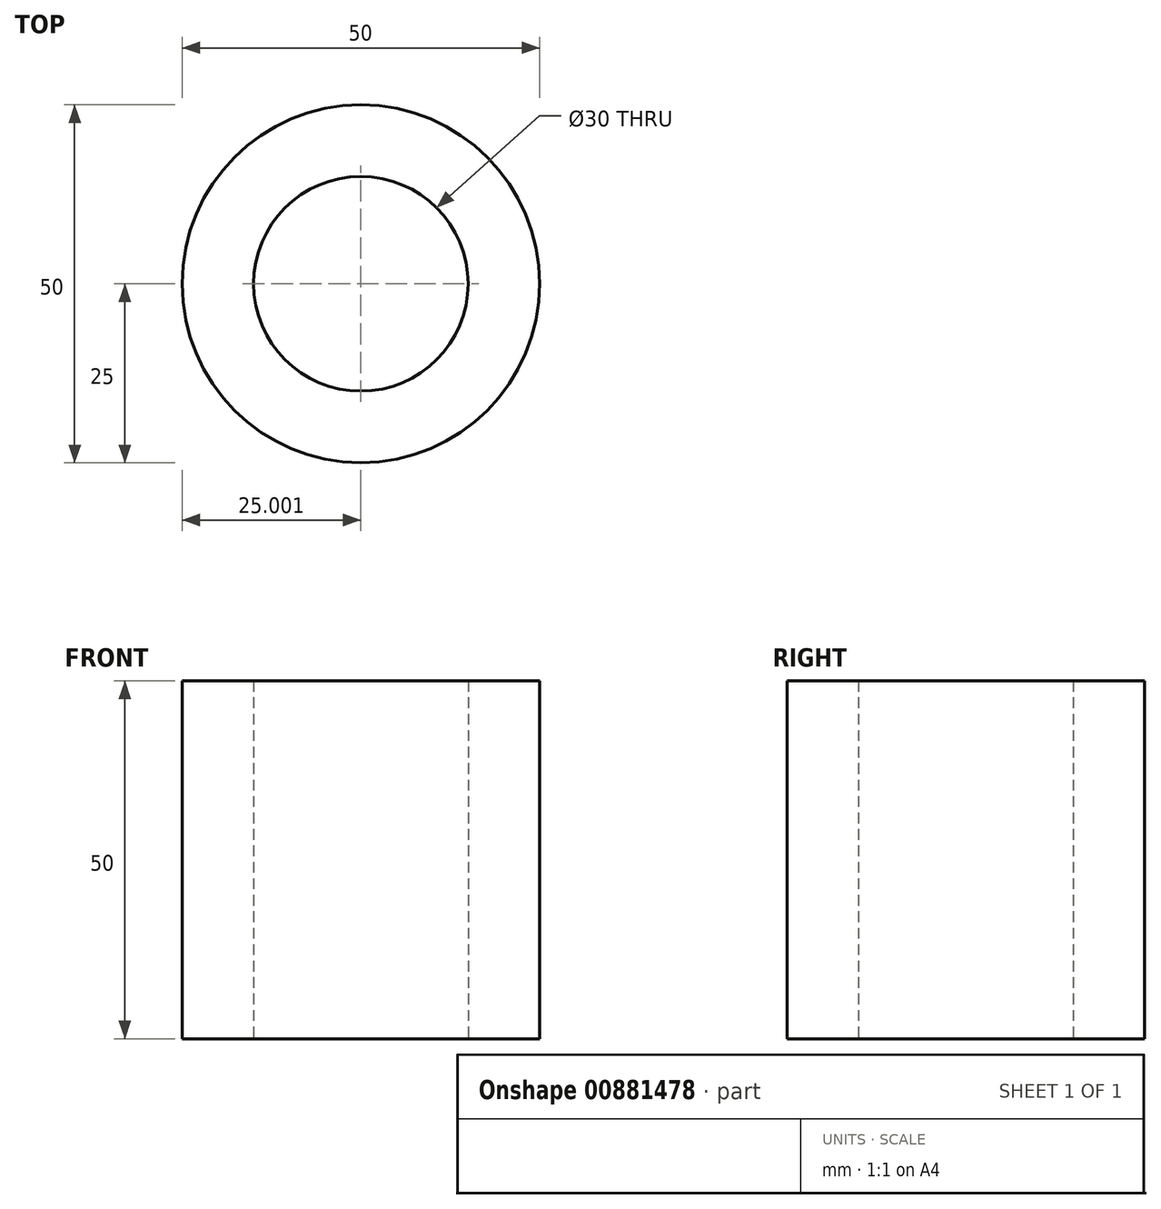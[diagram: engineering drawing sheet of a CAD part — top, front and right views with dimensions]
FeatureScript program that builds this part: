
annotation { "Feature Type Name" : "Feature", "Feature Type Description" : "" }
export const myFeature = defineFeature(function(context is Context, id is Id, definition is map)
    precondition{}
    {
        {
            var Q0;
            Q0=qCreatedBy(makeId("Top.planeOp"),FACE);
            var sketch = newSketch(context, id + "F0", { "sketchPlane" : qUnion([Q0])});
            skCircle(sketch, "E0", {"center": v(-44.73, 0) * mm, "radius": 15 * mm});
            skCircle(sketch, "E1.0", {"center": v(-44.73, 0) * mm, "radius": 25 * mm});
            skSolve(sketch);
        }
        {
            var Q0;
            Q0 = qSketchRegion(id + "F0", true);
            extrude(context, id + "F1", {"entities" : qUnion([Q0]), "depth" : 50 * mm, "offsetDistance" : 25 * mm});
        }
    });
